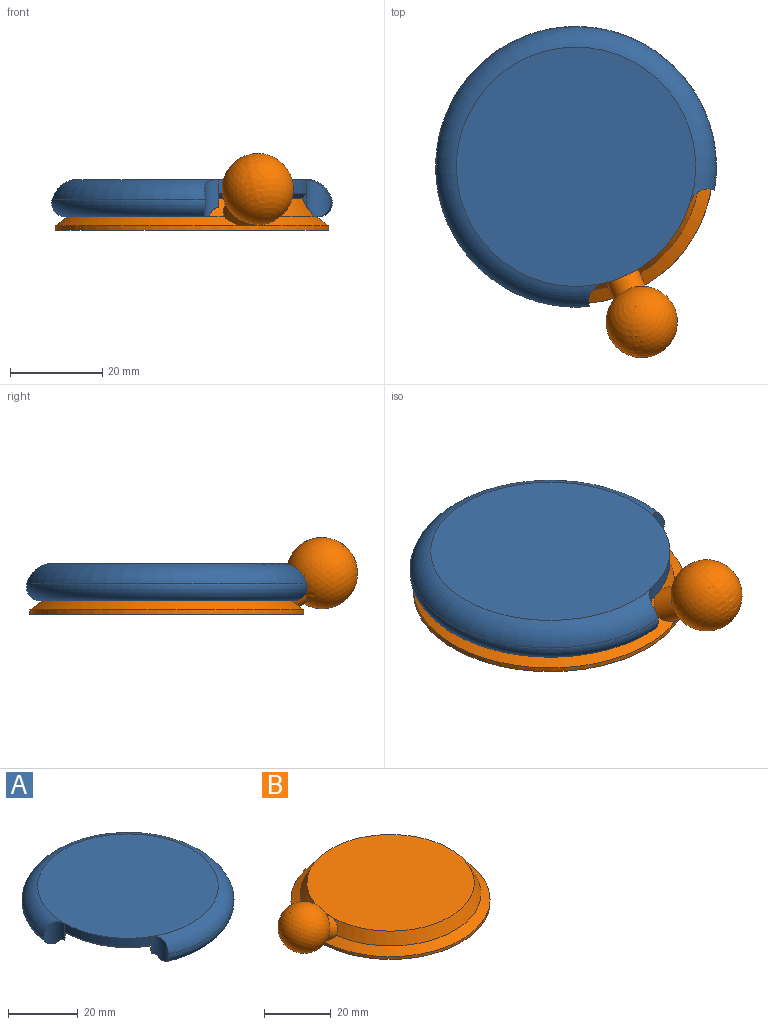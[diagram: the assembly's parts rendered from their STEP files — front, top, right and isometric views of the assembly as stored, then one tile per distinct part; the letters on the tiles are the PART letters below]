
ASSEMBLY  parts=2 mates=1
PART A: 11 faces, bbox 66.3x66.3x8.2 mm
  f0: torus R=24.61mm, axis (0,0,1), area 916.6mm2, adj f1,f4,f8,f9
  f1: torus R=27.5mm, axis (0,0,1), area 880.4mm2, adj f0,f2,f8,f9
  f2: cone r=25mm half-angle=26.6deg, axis (0,0,-1), area 601.2mm2, adj f1,f3,f6,f7,f8,f9
  f3: plane 50x50mm, normal (0,0,-1), area 1963.5mm2, adj f2,f10
  f4: plane 52x52mm, normal (0,0,1), area 2123.7mm2, adj f0,f5
  f5: cylinder r=26mm len=22.52mm, axis (0,0,-1), area 81.7mm2, adj f4,f8,f9,f10
  f6: plane 3x0.87mm, normal (-0.87,0.5,0), area 1.5mm2, adj f2,f9,f10
  f7: plane 3x1mm, normal (0,-1,0), area 1.5mm2, adj f2,f8,f10
  f8: cylinder r=4mm len=8.04mm, axis (0,0,1), area 40.1mm2, adj f0,f1,f2,f5,f7
  f9: cylinder r=4mm len=8.04mm, axis (0,0,1), area 40.1mm2, adj f0,f1,f2,f5,f6
  f10: cone r=25mm half-angle=45deg, axis (0,0,1), area 37.8mm2, adj f3,f5,f6,f7
PART B: 9 faces, bbox 74.2x59.6x16.8 mm
  f0: cylinder r=3.75mm len=8.86mm, axis (0.88,0,-0.48), area 98.1mm2, adj f2,f3,f8
  f1: plane 59.55x59.55mm, normal (0,0,-1), area 2780.5mm2, adj f4,f6,f7
  f2: cone r=27mm half-angle=26.6deg, axis (0,0,-1), area 703.5mm2, adj f0,f3,f5
  f3: cone r=29.75mm half-angle=54deg, axis (0,0,-1), area 587.2mm2, adj f0,f2,f4
  f4: cylinder r=29.75mm len=59.5mm, axis (0,0,1), area 186.9mm2, adj f1,f3
  f5: plane 50x50mm, normal (0,0,1), area 1963.5mm2, adj f2
  f6: cylinder r=3.75mm len=0.65mm, axis (0.88,0,-0.48), area 0mm2, adj f1,f7
  f7: plane 0.65x0.01mm, normal (0.88,0,-0.48), area 0mm2, adj f1,f6
  f8: sphere r=7.75mm, area 707.6mm2, adj f0
PLACE A rot(axis=(0,0,1),102.9deg) t=(45.18,-0.57,-3.48)mm
PLACE B rot(axis=(0,0,1),112.9deg) t=(46.07,-0.29,18.04)mm
MATE revolute B.f4 <-> A.f5  axis (0,0,1) through (43.99,4.63,-8.37)mm
